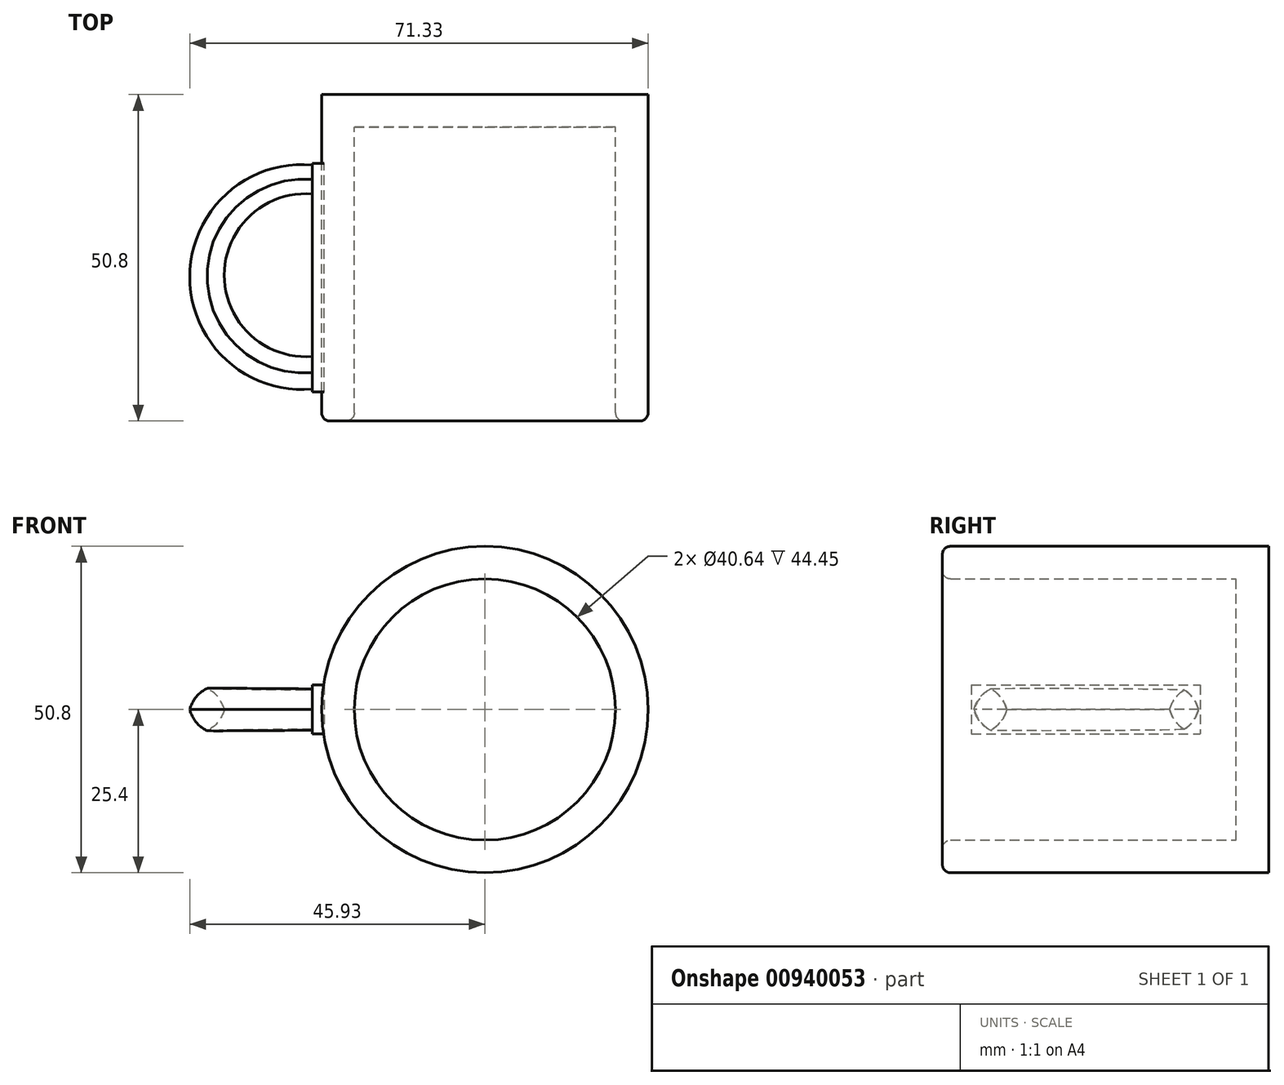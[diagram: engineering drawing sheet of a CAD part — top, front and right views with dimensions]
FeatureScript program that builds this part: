
annotation { "Feature Type Name" : "Feature", "Feature Type Description" : "" }
export const myFeature = defineFeature(function(context is Context, id is Id, definition is map)
    precondition{}
    {
        {
            var Q0;
            Q0=qCreatedBy(makeId("Front.planeOp"),FACE);
            var sketch = newSketch(context, id + "F0", { "sketchPlane" : qUnion([Q0])});
            skCircle(sketch, "E0", {"center": v(0, 0) * mm, "radius": 25.4 * mm});
            skSolve(sketch);
        }
        {
            var Q0;
            Q0 = qSketchRegion(id + "F0", true);
            extrude(context, id + "F1", {"entities" : qUnion([Q0]), "depth" : 50.8 * mm, "offsetDistance" : 25.4 * mm});
        }
        {
            var Q0;
            Q0=makeQuery(id+"F1.opExtrude","CAP_FACE",FACE,{"disambiguationData":[OSD([sQuery(id+"F0.wireOp",EDGE,"E0")])],"isStart":false});
            shell(context, id + "F2", {"entities" : qUnion([Q0]), "thickness" : 5.08 * mm});
        }
        {
            var Q0;
            Q0=makeQuery(id+"F1.opExtrude","CAP_FACE",FACE,{"disambiguationData":[OSD([sQuery(id+"F0.wireOp",EDGE,"E0")])],"isStart":false});
            fillet(context, id + "F3", {"entities" : qUnion([Q0]), "radius" : 1.27 * mm, "tangentPropagation" : true, "allowEdgeOverflow" : false});
        }
        {
            var Q0;
            Q0=qCreatedBy(makeId("Top.planeOp"),FACE);
            var sketch = newSketch(context, id + "F4", { "sketchPlane" : qUnion([Q0])});
            skPoint(sketch, "E1", {"position": v(-26.89, -15.62) * mm});
            skPoint(sketch, "E2", {"position": v(-26.89, -40.59) * mm});
            skArc(sketch, "E3", {"start": v(-26.89, -15.62) * mm, "mid": v(-40.4, -28.1) * mm, "end": v(-26.89, -40.59) * mm});
            skPoint(sketch, "E4", {"position": v(-26.89, -46) * mm});
            skPoint(sketch, "E5", {"position": v(-26.89, -10.8) * mm});
            skArc(sketch, "E6", {"start": v(-26.89, -10.8) * mm, "mid": v(-46.09, -28.4) * mm, "end": v(-26.89, -46) * mm});
            skLineSegment(sketch, "E7", {"start": v(-26.89, -15.62) * mm, "end": v(-26.89, -10.8) * mm});
            skLineSegment(sketch, "E8", {"start": v(-26.89, -40.59) * mm, "end": v(-26.89, -46) * mm});
            skSolve(sketch);
        }
        {
            var Q0;
            Q0 = qSketchRegion(id + "F4", true);
            extrude(context, id + "F5", {"entities" : qUnion([Q0]), "depth" : 7.62 * mm, "offsetDistance" : 25.4 * mm, "symmetric" : true});
        }
        {
            var Q0;
            Q0=qCreatedBy(makeId("Top.planeOp"),FACE);
            var sketch = newSketch(context, id + "F6", { "sketchPlane" : qUnion([Q0])});
            skLineSegment(sketch, "E9.bottom", {"start": v(-26.88, -46.27) * mm, "end": v(-25.04, -46.27) * mm});
            skLineSegment(sketch, "E9.top", {"start": v(-26.88, -10.71) * mm, "end": v(-25.04, -10.71) * mm});
            skLineSegment(sketch, "E9.left", {"start": v(-26.88, -46.27) * mm, "end": v(-26.88, -10.71) * mm});
            skLineSegment(sketch, "E9.right", {"start": v(-25.04, -46.27) * mm, "end": v(-25.04, -10.71) * mm});
            skSolve(sketch);
        }
        {
            var Q0;
            Q0 = qSketchRegion(id + "F6", true);
            extrude(context, id + "F7", {"entities" : qUnion([Q0]), "depth" : 7.62 * mm, "offsetDistance" : 25.4 * mm, "symmetric" : true});
        }
        {
            var Q0;
            Q0=makeQuery(id+"F5.opExtrude","CAP_EDGE",EDGE,{"disambiguationData":[OSD([sQuery(id+"F4.wireOp",EDGE,"E3")])],"isStart":true});
            var Q1;
            Q1=makeQuery(id+"F5.opExtrude","CAP_EDGE",EDGE,{"disambiguationData":[OSD([sQuery(id+"F4.wireOp",EDGE,"E3")])],"isStart":false});
            var Q2;
            Q2=makeQuery(id+"F5.opExtrude","CAP_EDGE",EDGE,{"disambiguationData":[OSD([sQuery(id+"F4.wireOp",EDGE,"E6")])],"isStart":true});
            var Q3;
            Q3=makeQuery(id+"F5.opExtrude","CAP_EDGE",EDGE,{"disambiguationData":[OSD([sQuery(id+"F4.wireOp",EDGE,"E6")])],"isStart":false});
            fillet(context, id + "F8", {"entities" : qUnion([Q0, Q1, Q2, Q3]), "radius" : 5.08 * mm, "tangentPropagation" : true, "allowEdgeOverflow" : false});
        }
    });
